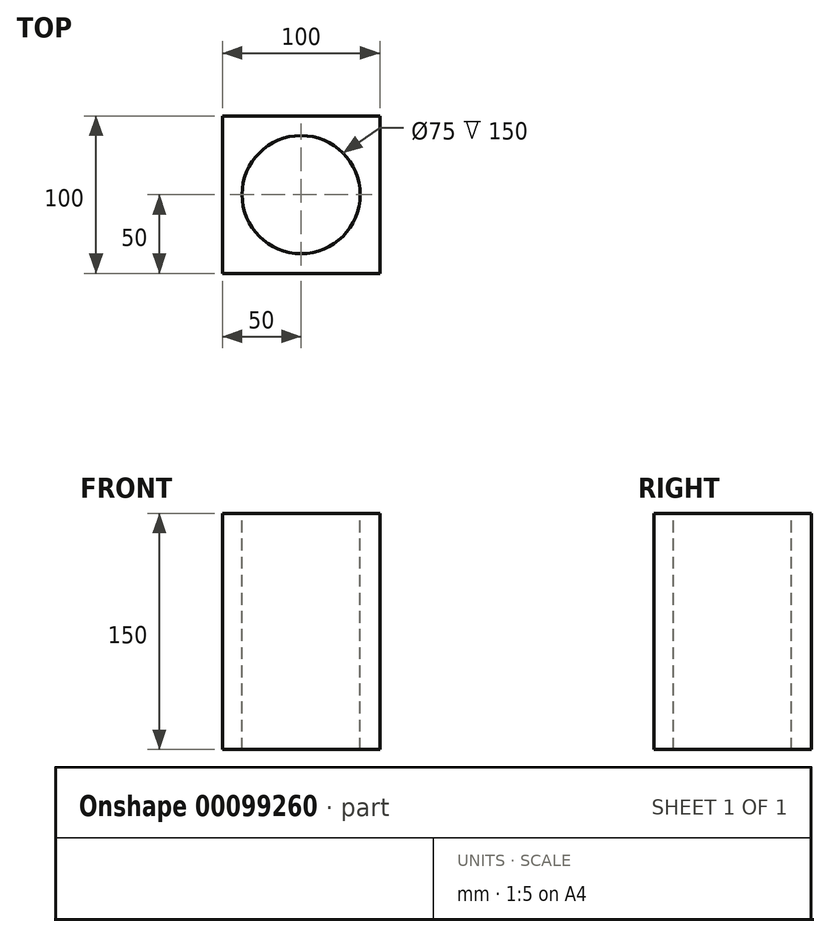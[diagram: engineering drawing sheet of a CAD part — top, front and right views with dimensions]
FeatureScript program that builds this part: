
annotation { "Feature Type Name" : "Feature", "Feature Type Description" : "" }
export const myFeature = defineFeature(function(context is Context, id is Id, definition is map)
    precondition{}
    {
        {
            var Q0;
            Q0=qCreatedBy(makeId("Top.planeOp"),FACE);
            var sketch = newSketch(context, id + "F0", { "sketchPlane" : qUnion([Q0])});
            skLineSegment(sketch, "E0.bottom", {"start": v(50, 50) * mm, "end": v(-50, 50) * mm});
            skLineSegment(sketch, "E0.top", {"start": v(50, -50) * mm, "end": v(-50, -50) * mm});
            skLineSegment(sketch, "E0.left", {"start": v(50, 50) * mm, "end": v(50, -50) * mm});
            skLineSegment(sketch, "E0.right", {"start": v(-50, 50) * mm, "end": v(-50, -50) * mm});
            skPoint(sketch, "E0.middle", {"position": v(0, 0) * mm});
            skSolve(sketch);
        }
        {
            var Q0;
            Q0 = qSketchRegion(id + "F0", true);
            extrude(context, id + "F1", {"entities" : qUnion([Q0]), "endBound" : BoundingType.SYMMETRIC, "depth" : 150 * mm});
        }
        {
            var Q0;
            Q0=makeQuery(id+"F1.opExtrude","CAP_FACE",FACE,{"disambiguationData":[OSD([sQuery(id+"F0.wireOp",EDGE,"E0.bottom"),sQuery(id+"F0.wireOp",EDGE,"E0.top"),sQuery(id+"F0.wireOp",EDGE,"E0.left"),sQuery(id+"F0.wireOp",EDGE,"E0.right")])],"isStart":false});
            var sketch = newSketch(context, id + "F2", { "sketchPlane" : qUnion([Q0])});
            skCircle(sketch, "E1", {"center": v(0, 0) * mm, "radius": 37.5 * mm});
            skSolve(sketch);
        }
        {
            var Q0;
            Q0 = qSketchRegion(id + "F2", true);
            extrude(context, id + "F3", {"entities" : qUnion([Q0]), "operationType" : NewBodyOperationType.REMOVE, "endBound" : BoundingType.THROUGH_ALL, "oppositeDirection" : true, "depth" : 25 * mm});
        }
    });
